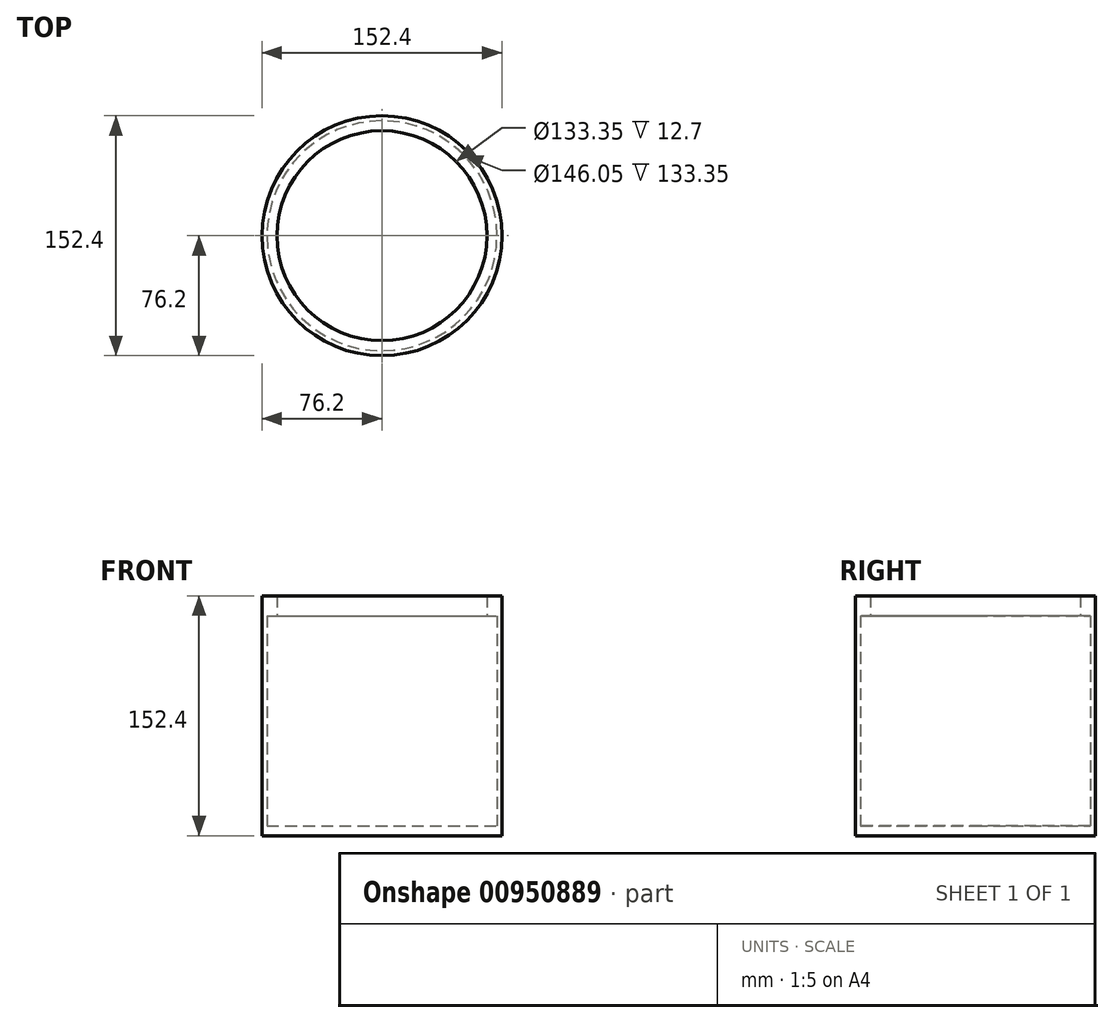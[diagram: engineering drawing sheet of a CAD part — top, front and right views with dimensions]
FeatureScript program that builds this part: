
annotation { "Feature Type Name" : "Feature", "Feature Type Description" : "" }
export const myFeature = defineFeature(function(context is Context, id is Id, definition is map)
    precondition{}
    {
        {
            var Q0;
            Q0=qCreatedBy(makeId("Front.planeOp"),FACE);
            var sketch = newSketch(context, id + "F0", { "sketchPlane" : qUnion([Q0])});
            skLineSegment(sketch, "E0", {"start": v(0, 129.02) * mm, "end": v(0, -117.04) * mm, "construction": true});
            skLineSegment(sketch, "E1", {"start": v(0, -80) * mm, "end": v(-76.2, -80) * mm});
            skLineSegment(sketch, "E2", {"start": v(-76.2, -80) * mm, "end": v(-76.2, 72.4) * mm});
            skLineSegment(sketch, "E3", {"start": v(-76.2, 72.4) * mm, "end": v(-66.67, 72.4) * mm});
            skLineSegment(sketch, "E4", {"start": v(-66.68, 72.4) * mm, "end": v(-66.68, 59.7) * mm});
            skLineSegment(sketch, "E5", {"start": v(-66.67, 59.7) * mm, "end": v(-73.03, 59.7) * mm});
            skLineSegment(sketch, "E6", {"start": v(-73.03, 59.7) * mm, "end": v(-73.02, -73.65) * mm});
            skLineSegment(sketch, "E7", {"start": v(-73.02, -73.65) * mm, "end": v(0, -73.65) * mm});
            skSolve(sketch);
        }
        {
            var Q0;
            Q0=sQuery(id+"F0.wireOp",EDGE,"E6");
            var Q1;
            Q1=sQuery(id+"F0.wireOp",EDGE,"E4");
            var Q2;
            Q2=sQuery(id+"F0.wireOp",EDGE,"E3");
            var Q3;
            Q3=sQuery(id+"F0.wireOp",EDGE,"E2");
            var Q4;
            Q4=sQuery(id+"F0.wireOp",EDGE,"E1");
            var Q5;
            Q5=sQuery(id+"F0.wireOp",EDGE,"E7");
            var Q6;
            Q6=sQuery(id+"F0.wireOp",EDGE,"E5");
            var Q7;
            Q7=sQuery(id+"F0.wireOp",EDGE,"E0");
            revolve(context, id + "F1", {"bodyType" : ToolBodyType.SURFACE, "surfaceOperationType" : NewSurfaceOperationType.NEW, "surfaceEntities" : qUnion([Q0, Q1, Q2, Q3, Q4, Q5, Q6]), "axis" : qUnion([Q7]), "revolveType" : RevolveType.FULL});
        }
    });
